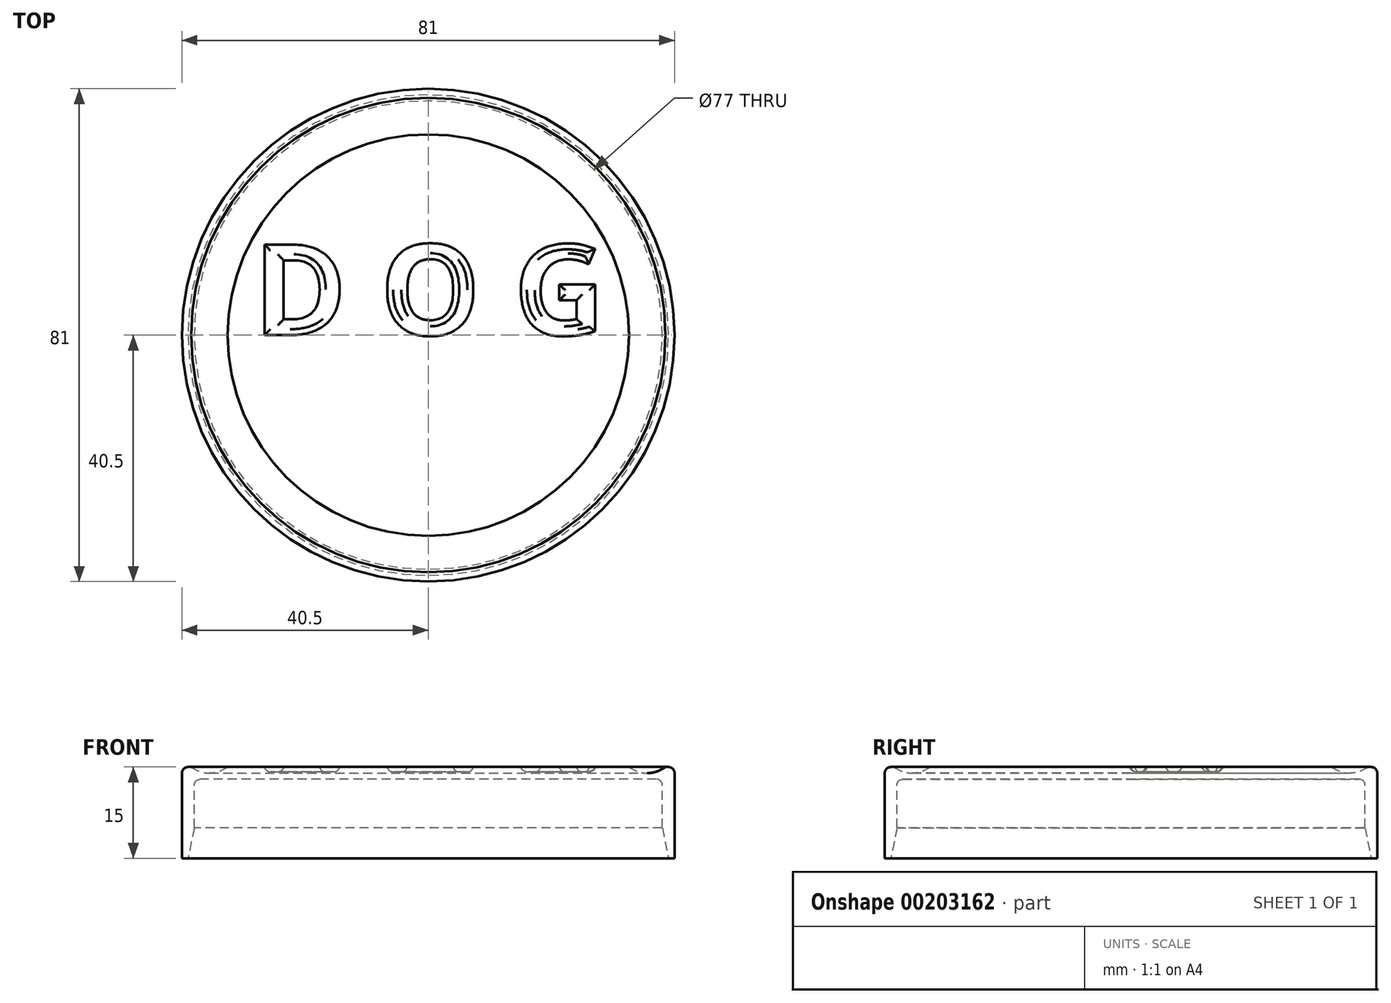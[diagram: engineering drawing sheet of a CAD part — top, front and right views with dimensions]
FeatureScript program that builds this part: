
annotation { "Feature Type Name" : "Feature", "Feature Type Description" : "" }
export const myFeature = defineFeature(function(context is Context, id is Id, definition is map)
    precondition{}
    {
        {
            var Q0;
            Q0=qCreatedBy(makeId("Top.planeOp"),FACE);
            var sketch = newSketch(context, id + "F0", { "sketchPlane" : qUnion([Q0])});
            skCircle(sketch, "E0", {"center": v(0, 0) * mm, "radius": 40.5 * mm});
            skCircle(sketch, "E1", {"center": v(0, 0) * mm, "radius": 38.5 * mm});
            skText(sketch, "E2", { "text": "D O G ", "fontName": "OpenSans-Bold.ttf"});
            const initialGuessF0  = {"E2": [-0.0288, 0, 1, 0, 0.015]};
            skSetInitialGuess(sketch, initialGuessF0);
            skSolve(sketch);
        }
        {
            var Q0;
            Q0=makeQuery(id+"F0.imprint","IMPRINT",FACE,{"disambiguationData":[TD([[makeQuery(id+"F0.imprint","IMPRINT",EDGE,{"derivedFrom":sQuery(id+"F0.wireOp",EDGE,"E0")}),1.0]])]});
            extrude(context, id + "F1", {"entities" : qUnion([Q0]), "oppositeDirection" : true, "depth" : 15 * mm});
        }
        {
            var Q0;
            Q0=makeQuery(id+"F0.imprint","IMPRINT",FACE,{"disambiguationData":[TD([[makeQuery(id+"F0.imprint","IMPRINT",EDGE,{"derivedFrom":sQuery(id+"F0.wireOp",EDGE,"E1")}),1.0]])]});
            var Q1;
            Q1 = qSketchRegion(id + "F0", true);
            var Q2;
            Q2=makeQuery(id+"F0.imprint","IMPRINT",FACE,{"disambiguationData":[TD([[makeQuery(id+"F0.imprint","IMPRINT",EDGE,{"derivedFrom":sQuery(id+"F0.wireOp",EDGE,"E2.sketch_text.stroke-12")}),-1.0]])]});
            var Q3;
            Q3=makeQuery(id+"F0.imprint","IMPRINT",FACE,{"disambiguationData":[TD([[makeQuery(id+"F0.imprint","IMPRINT",EDGE,{"derivedFrom":sQuery(id+"F0.wireOp",EDGE,"E2.sketch_text.stroke-0")}),-1.0]])]});
            var Q4;
            Q4=makeQuery(id+"F0.imprint","IMPRINT",FACE,{"disambiguationData":[TD([[makeQuery(id+"F0.imprint","IMPRINT",EDGE,{"derivedFrom":sQuery(id+"F0.wireOp",EDGE,"E2.sketch_text.stroke-26")}),-1.0]])]});
            var Q5;
            Q5=makeQuery(id+"F0.imprint","IMPRINT",FACE,{"disambiguationData":[TD([[makeQuery(id+"F0.imprint","IMPRINT",EDGE,{"derivedFrom":sQuery(id+"F0.wireOp",EDGE,"E2.sketch_text.stroke-20")}),1.0]])]});
            var Q6;
            Q6=makeQuery(id+"F0.imprint","IMPRINT",FACE,{"disambiguationData":[TD([[makeQuery(id+"F0.imprint","IMPRINT",EDGE,{"derivedFrom":sQuery(id+"F0.wireOp",EDGE,"E2.sketch_text.stroke-7")}),1.0]])]});
            extrude(context, id + "F2", {"entities" : qUnion([Q0, Q1, Q2, Q3, Q4, Q5, Q6]), "operationType" : NewBodyOperationType.ADD, "oppositeDirection" : true, "depth" : 2 * mm});
        }
        {
            var Q0;
            Q0=makeQuery(id+"F0.imprint","IMPRINT",FACE,{"disambiguationData":[TD([[makeQuery(id+"F0.imprint","IMPRINT",EDGE,{"derivedFrom":sQuery(id+"F0.wireOp",EDGE,"E2.sketch_text.stroke-0")}),-1.0]])]});
            var Q1;
            Q1=makeQuery(id+"F0.imprint","IMPRINT",FACE,{"disambiguationData":[TD([[makeQuery(id+"F0.imprint","IMPRINT",EDGE,{"derivedFrom":sQuery(id+"F0.wireOp",EDGE,"E2.sketch_text.stroke-12")}),-1.0]])]});
            var Q2;
            Q2=makeQuery(id+"F0.imprint","IMPRINT",FACE,{"disambiguationData":[TD([[makeQuery(id+"F0.imprint","IMPRINT",EDGE,{"derivedFrom":sQuery(id+"F0.wireOp",EDGE,"E2.sketch_text.stroke-26")}),-1.0]])]});
            extrude(context, id + "F3", {"entities" : qUnion([Q0, Q1, Q2]), "operationType" : NewBodyOperationType.REMOVE, "oppositeDirection" : true, "depth" : .8 * mm});
        }
        {
            var Q0;
            Q0=makeQuery(id+"F1.opExtrude","CAP_EDGE",EDGE,{"disambiguationData":[OSD([sQuery(id+"F0.wireOp",EDGE,"E0")])],"isStart":true});
            fillet(context, id + "F4", {"entities" : qUnion([Q0]), "radius" : 1 * mm, "tangentPropagation" : true, "allowEdgeOverflow" : false});
        }
        {
            var Q0;
            Q0=makeQuery(id+"F1.opExtrude","CAP_EDGE",EDGE,{"disambiguationData":[OSD([sQuery(id+"F0.wireOp",EDGE,"E1")])],"isStart":false});
            chamfer(context, id + "F5", {"entities" : qUnion([Q0]), "chamferType" : ChamferType.TWO_OFFSETS, "width1" : 1 * mm, "oppositeDirection" : false, "width2" : 5 * mm, "tangentPropagation" : true});
        }
        {
            var Q0;
            Q0=qCreatedBy(makeId("Front.planeOp"),FACE);
            var sketch = newSketch(context, id + "F6", { "sketchPlane" : qUnion([Q0])});
            skLineSegment(sketch, "E3", {"start": v(38.5, -1) * mm, "end": v(38.5, -15) * mm});
            skLineSegment(sketch, "E4", {"start": v(-38.5, -15) * mm, "end": v(-38.5, -1) * mm});
            skLineSegment(sketch, "E5", {"start": v(0, -0.6) * mm, "end": v(0, 0) * mm});
            skLineSegment(sketch, "E6", {"start": v(38.5, 0) * mm, "end": v(38.5, -15) * mm});
            skLineSegment(sketch, "E7", {"start": v(-38.5, -15) * mm, "end": v(-38.5, 0) * mm});
            skLineSegment(sketch, "E8.0", {"start": v(-35, -15) * mm, "end": v(35, -15) * mm});
            skArc(sketch, "E9", {"start": v(-39, 0) * mm, "mid": v(-36, -1) * mm, "end": v(-33, 0) * mm});
            skLineSegment(sketch, "E10", {"start": v(-39, 0) * mm, "end": v(0, 0) * mm});
            skSolve(sketch);
        }
        {
            var Q0;
            {var subQ0=sQuery(id+"F6.wireOp",EDGE,"E10");var subQ1=sQuery(id+"F6.wireOp",EDGE,"E7");var subQ2=makeQuery(id+"F6.imprint","INTERSECT",VERTEX,{"derivedFrom":[subQ1,subQ0]});Q0=makeQuery(id+"F6.imprint","IMPRINT",FACE,{"disambiguationData":[TD([[makeQuery(id+"F6.imprint","IMPRINT",EDGE,{"disambiguationData":[TD([[subQ2,1.0]])],"derivedFrom":subQ1}),1.0]])]});}
            var Q1;
            {var subQ0=sQuery(id+"F6.wireOp",EDGE,"E10");var subQ1=sQuery(id+"F6.wireOp",EDGE,"E7");var subQ2=makeQuery(id+"F6.imprint","INTERSECT",VERTEX,{"derivedFrom":[subQ1,subQ0]});Q1=makeQuery(id+"F6.imprint","IMPRINT",FACE,{"disambiguationData":[TD([[makeQuery(id+"F6.imprint","IMPRINT",EDGE,{"disambiguationData":[TD([[subQ2,1.0]])],"derivedFrom":subQ1}),-1.0]])]});}
            var Q2;
            Q2=sQuery(id+"F0.wireOp",EDGE,"E1");
            revolve(context, id + "F7", {"operationType" : NewBodyOperationType.REMOVE, "entities" : qUnion([Q0, Q1]), "axis" : qUnion([Q2]), "revolveType" : RevolveType.FULL, "oppositeDirection" : true});
        }
        {
            var Q0;
            Q0=makeQuery(id+"F3.boolean.opBoolean","COPY",FACE,{"derivedFrom":makeQuery(id+"F3.opExtrude","CAP_FACE",FACE,{"disambiguationData":[OSD([sQuery(id+"F0.wireOp",EDGE,"E2.sketch_text.stroke-0"),sQuery(id+"F0.wireOp",EDGE,"E2.sketch_text.stroke-1"),sQuery(id+"F0.wireOp",EDGE,"E2.sketch_text.stroke-2"),sQuery(id+"F0.wireOp",EDGE,"E2.sketch_text.stroke-3"),sQuery(id+"F0.wireOp",EDGE,"E2.sketch_text.stroke-4"),sQuery(id+"F0.wireOp",EDGE,"E2.sketch_text.stroke-5"),sQuery(id+"F0.wireOp",EDGE,"E2.sketch_text.stroke-6"),sQuery(id+"F0.wireOp",EDGE,"E2.sketch_text.stroke-7"),sQuery(id+"F0.wireOp",EDGE,"E2.sketch_text.stroke-8"),sQuery(id+"F0.wireOp",EDGE,"E2.sketch_text.stroke-9"),sQuery(id+"F0.wireOp",EDGE,"E2.sketch_text.stroke-10"),sQuery(id+"F0.wireOp",EDGE,"E2.sketch_text.stroke-11")])],"isStart":false})});
            var Q1;
            Q1=makeQuery(id+"F3.boolean.opBoolean","COPY",FACE,{"derivedFrom":makeQuery(id+"F3.opExtrude","CAP_FACE",FACE,{"disambiguationData":[OSD([sQuery(id+"F0.wireOp",EDGE,"E2.sketch_text.stroke-12"),sQuery(id+"F0.wireOp",EDGE,"E2.sketch_text.stroke-13"),sQuery(id+"F0.wireOp",EDGE,"E2.sketch_text.stroke-14"),sQuery(id+"F0.wireOp",EDGE,"E2.sketch_text.stroke-15"),sQuery(id+"F0.wireOp",EDGE,"E2.sketch_text.stroke-16"),sQuery(id+"F0.wireOp",EDGE,"E2.sketch_text.stroke-17"),sQuery(id+"F0.wireOp",EDGE,"E2.sketch_text.stroke-18"),sQuery(id+"F0.wireOp",EDGE,"E2.sketch_text.stroke-19"),sQuery(id+"F0.wireOp",EDGE,"E2.sketch_text.stroke-20"),sQuery(id+"F0.wireOp",EDGE,"E2.sketch_text.stroke-21"),sQuery(id+"F0.wireOp",EDGE,"E2.sketch_text.stroke-22"),sQuery(id+"F0.wireOp",EDGE,"E2.sketch_text.stroke-23"),sQuery(id+"F0.wireOp",EDGE,"E2.sketch_text.stroke-24"),sQuery(id+"F0.wireOp",EDGE,"E2.sketch_text.stroke-25")])],"isStart":false})});
            var Q2;
            Q2=makeQuery(id+"F3.boolean.opBoolean","COPY",FACE,{"derivedFrom":makeQuery(id+"F3.opExtrude","CAP_FACE",FACE,{"disambiguationData":[OSD([sQuery(id+"F0.wireOp",EDGE,"E2.sketch_text.stroke-26"),sQuery(id+"F0.wireOp",EDGE,"E2.sketch_text.stroke-27"),sQuery(id+"F0.wireOp",EDGE,"E2.sketch_text.stroke-28"),sQuery(id+"F0.wireOp",EDGE,"E2.sketch_text.stroke-29"),sQuery(id+"F0.wireOp",EDGE,"E2.sketch_text.stroke-30"),sQuery(id+"F0.wireOp",EDGE,"E2.sketch_text.stroke-31"),sQuery(id+"F0.wireOp",EDGE,"E2.sketch_text.stroke-32"),sQuery(id+"F0.wireOp",EDGE,"E2.sketch_text.stroke-33"),sQuery(id+"F0.wireOp",EDGE,"E2.sketch_text.stroke-34"),sQuery(id+"F0.wireOp",EDGE,"E2.sketch_text.stroke-35"),sQuery(id+"F0.wireOp",EDGE,"E2.sketch_text.stroke-36"),sQuery(id+"F0.wireOp",EDGE,"E2.sketch_text.stroke-37"),sQuery(id+"F0.wireOp",EDGE,"E2.sketch_text.stroke-38"),sQuery(id+"F0.wireOp",EDGE,"E2.sketch_text.stroke-39"),sQuery(id+"F0.wireOp",EDGE,"E2.sketch_text.stroke-40"),sQuery(id+"F0.wireOp",EDGE,"E2.sketch_text.stroke-41"),sQuery(id+"F0.wireOp",EDGE,"E2.sketch_text.stroke-42"),sQuery(id+"F0.wireOp",EDGE,"E2.sketch_text.stroke-43"),sQuery(id+"F0.wireOp",EDGE,"E2.sketch_text.stroke-44")])],"isStart":false})});
            fillet(context, id + "F8", {"entities" : qUnion([Q0, Q1, Q2]), "radius" : 1 * mm, "tangentPropagation" : true, "allowEdgeOverflow" : false});
        }
        {
            var Q0;
            Q0=makeQuery(id+"F2.boolean.opBoolean","INTERSECT",EDGE,{"derivedFrom":[makeQuery(id+"F1.opExtrude","SWEPT_FACE",FACE,{"disambiguationData":[OSD([sQuery(id+"F0.wireOp",EDGE,"E1")])]}),makeQuery(id+"F2.opExtrude","CAP_FACE",FACE,{"disambiguationData":[OSD([sQuery(id+"F0.wireOp",EDGE,"E0")])],"isStart":false})]});
            fillet(context, id + "F9", {"entities" : qUnion([Q0]), "radius" : 1 * mm, "tangentPropagation" : true, "allowEdgeOverflow" : false});
        }
    });
